# Revit family: b8eb4f78_b1b3_4f44_b286_0b090fb55ccd
name_source: partatom
category: Generic Models
revit_build: Autodesk Revit Architecture 2015 (Build: 20140606_1530(x64)
units: mm (PartAtom-declared; Revit-internal decimal feet)

## types (1)
- Default
    BIMobject category = Chairs, Stools & Benches
    BOSUseNativeGeometries = 0
    Design country = Sweden
    Edition number = 1
    IFC Classification = Furniture
    Manufacturer country = Sweden
    Manufacturer name = Scandinavian Business Seating
    Material main = Polypropylene
    Material secondary = Metal
    NBS Reference Code = 31-12
    NBS Reference Description = Chairs, Seats And Bench Seating
    Nominal height = 0
    Nominal width = 0
    Product Guid = ccc38254-2d4f-4d0e-8f1b-b286eb994f18
    Product SKU = RBMNoorUp6090
    Product data url = https://bimobject.com
    Product family = Canteen and conference chairs
    Product group = RBM Bella
    Product name = RBM Noor Up 6090
    QR code = http://bimobject.com
    UNSPSC Code = 56
    Uniclass 1.4 Code = L8222
    Uniclass 1.4 Description = Chairs
    Uniclass 2.0 Code = PR-31-12
    Uniclass 2.0 Description = Chairs, Seats And Bench Seating
    Weight Net (Kg) = 0

## geometry (parser evidence)
native form markers: Sweep x3
no freeform markers — native parametric forms only
